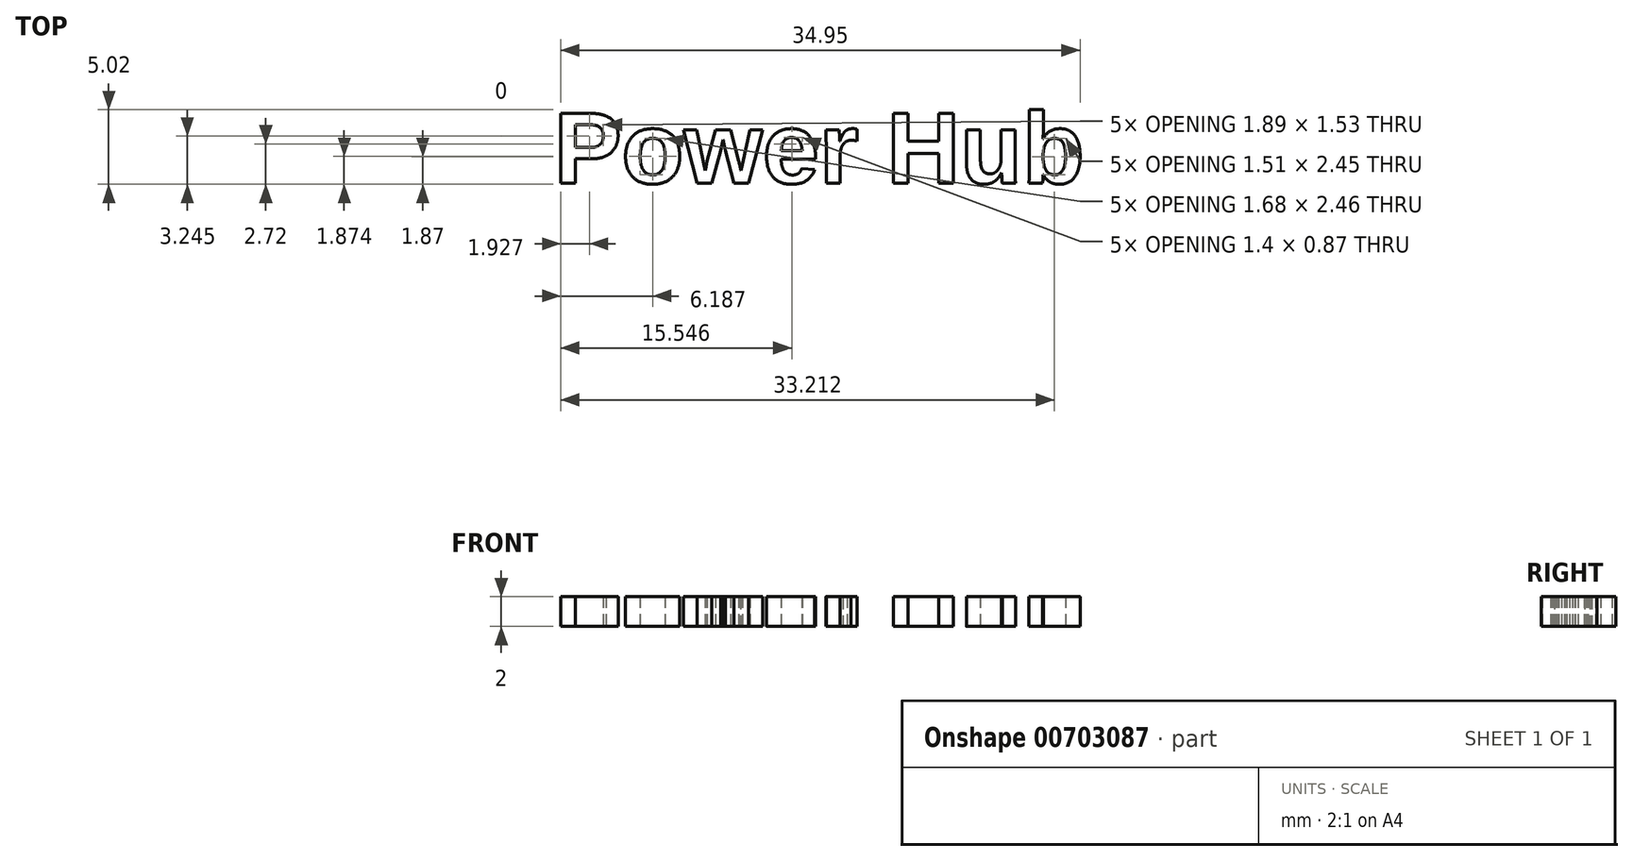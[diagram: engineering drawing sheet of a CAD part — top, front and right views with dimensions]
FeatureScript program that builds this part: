
annotation { "Feature Type Name" : "Feature", "Feature Type Description" : "" }
export const myFeature = defineFeature(function(context is Context, id is Id, definition is map)
    precondition{}
    {
        {
            var Q0;
            Q0=qCreatedBy(makeId("Top.planeOp"),FACE);
            var sketch = newSketch(context, id + "F0", { "sketchPlane" : qUnion([Q0])});
            skText(sketch, "E0", { "text": "Power Hub", "fontName": "Arimo-Bold.ttf"});
            const initialGuessF0  = {"E0": [0.01222, -0.00286, 1, 0, 0.00492]};
            skSetInitialGuess(sketch, initialGuessF0);
            skSolve(sketch);
        }
        {
            var Q0;
            Q0 = qSketchRegion(id + "F0", true);
            var Q1;
            Q1=makeQuery(id+"F0.imprint","IMPRINT",FACE,{"disambiguationData":[TD([[makeQuery(id+"F0.imprint","IMPRINT",EDGE,{"derivedFrom":sQuery(id+"F0.wireOp",EDGE,"c4a77d2d-5a0c-4d62-8845-47beaf8ddbdb.sketch_text.stroke-30")}),-1.0]])]});
            var Q2;
            Q2=makeQuery(id+"F0.imprint","IMPRINT",FACE,{"disambiguationData":[TD([[makeQuery(id+"F0.imprint","IMPRINT",EDGE,{"derivedFrom":sQuery(id+"F0.wireOp",EDGE,"c4a77d2d-5a0c-4d62-8845-47beaf8ddbdb.sketch_text.stroke-67")}),-1.0]])]});
            var Q3;
            Q3=makeQuery(id+"F0.imprint","IMPRINT",FACE,{"disambiguationData":[TD([[makeQuery(id+"F0.imprint","IMPRINT",EDGE,{"derivedFrom":sQuery(id+"F0.wireOp",EDGE,"c4a77d2d-5a0c-4d62-8845-47beaf8ddbdb.sketch_text.stroke-84")}),-1.0]])]});
            var Q4;
            Q4=makeQuery(id+"F0.imprint","IMPRINT",FACE,{"disambiguationData":[TD([[makeQuery(id+"F0.imprint","IMPRINT",EDGE,{"derivedFrom":sQuery(id+"F0.wireOp",EDGE,"c4a77d2d-5a0c-4d62-8845-47beaf8ddbdb.sketch_text.stroke-96")}),-1.0]])]});
            var Q5;
            Q5=makeQuery(id+"F0.imprint","IMPRINT",FACE,{"disambiguationData":[TD([[makeQuery(id+"F0.imprint","IMPRINT",EDGE,{"derivedFrom":sQuery(id+"F0.wireOp",EDGE,"c4a77d2d-5a0c-4d62-8845-47beaf8ddbdb.sketch_text.stroke-0")}),-1.0]])]});
            var Q6;
            Q6=makeQuery(id+"F0.imprint","IMPRINT",FACE,{"disambiguationData":[TD([[makeQuery(id+"F0.imprint","IMPRINT",EDGE,{"derivedFrom":sQuery(id+"F0.wireOp",EDGE,"c4a77d2d-5a0c-4d62-8845-47beaf8ddbdb.sketch_text.stroke-10")}),1.0]])]});
            var Q7;
            Q7=makeQuery(id+"F0.imprint","IMPRINT",FACE,{"disambiguationData":[TD([[makeQuery(id+"F0.imprint","IMPRINT",EDGE,{"derivedFrom":sQuery(id+"F0.wireOp",EDGE,"c4a77d2d-5a0c-4d62-8845-47beaf8ddbdb.sketch_text.stroke-16")}),-1.0]])]});
            var Q8;
            Q8=makeQuery(id+"F0.imprint","IMPRINT",FACE,{"disambiguationData":[TD([[makeQuery(id+"F0.imprint","IMPRINT",EDGE,{"derivedFrom":sQuery(id+"F0.wireOp",EDGE,"c4a77d2d-5a0c-4d62-8845-47beaf8ddbdb.sketch_text.stroke-24")}),1.0]])]});
            var Q9;
            Q9=makeQuery(id+"F0.imprint","IMPRINT",FACE,{"disambiguationData":[TD([[makeQuery(id+"F0.imprint","IMPRINT",EDGE,{"derivedFrom":sQuery(id+"F0.wireOp",EDGE,"c4a77d2d-5a0c-4d62-8845-47beaf8ddbdb.sketch_text.stroke-49")}),-1.0]])]});
            var Q10;
            Q10=makeQuery(id+"F0.imprint","IMPRINT",FACE,{"disambiguationData":[TD([[makeQuery(id+"F0.imprint","IMPRINT",EDGE,{"derivedFrom":sQuery(id+"F0.wireOp",EDGE,"c4a77d2d-5a0c-4d62-8845-47beaf8ddbdb.sketch_text.stroke-62")}),1.0]])]});
            var Q11;
            Q11=makeQuery(id+"F0.imprint","IMPRINT",FACE,{"disambiguationData":[TD([[makeQuery(id+"F0.imprint","IMPRINT",EDGE,{"derivedFrom":sQuery(id+"F0.wireOp",EDGE,"c4a77d2d-5a0c-4d62-8845-47beaf8ddbdb.sketch_text.stroke-113")}),-1.0]])]});
            var Q12;
            Q12=makeQuery(id+"F0.imprint","IMPRINT",FACE,{"disambiguationData":[TD([[makeQuery(id+"F0.imprint","IMPRINT",EDGE,{"derivedFrom":sQuery(id+"F0.wireOp",EDGE,"c4a77d2d-5a0c-4d62-8845-47beaf8ddbdb.sketch_text.stroke-130")}),1.0]])]});
            extrude(context, id + "F1", {"entities" : qUnion([Q0, Q1, Q2, Q3, Q4, Q5, Q6, Q7, Q8, Q9, Q10, Q11, Q12]), "depth" : 2 * mm, "offsetDistance" : 25 * mm});
        }
    });
